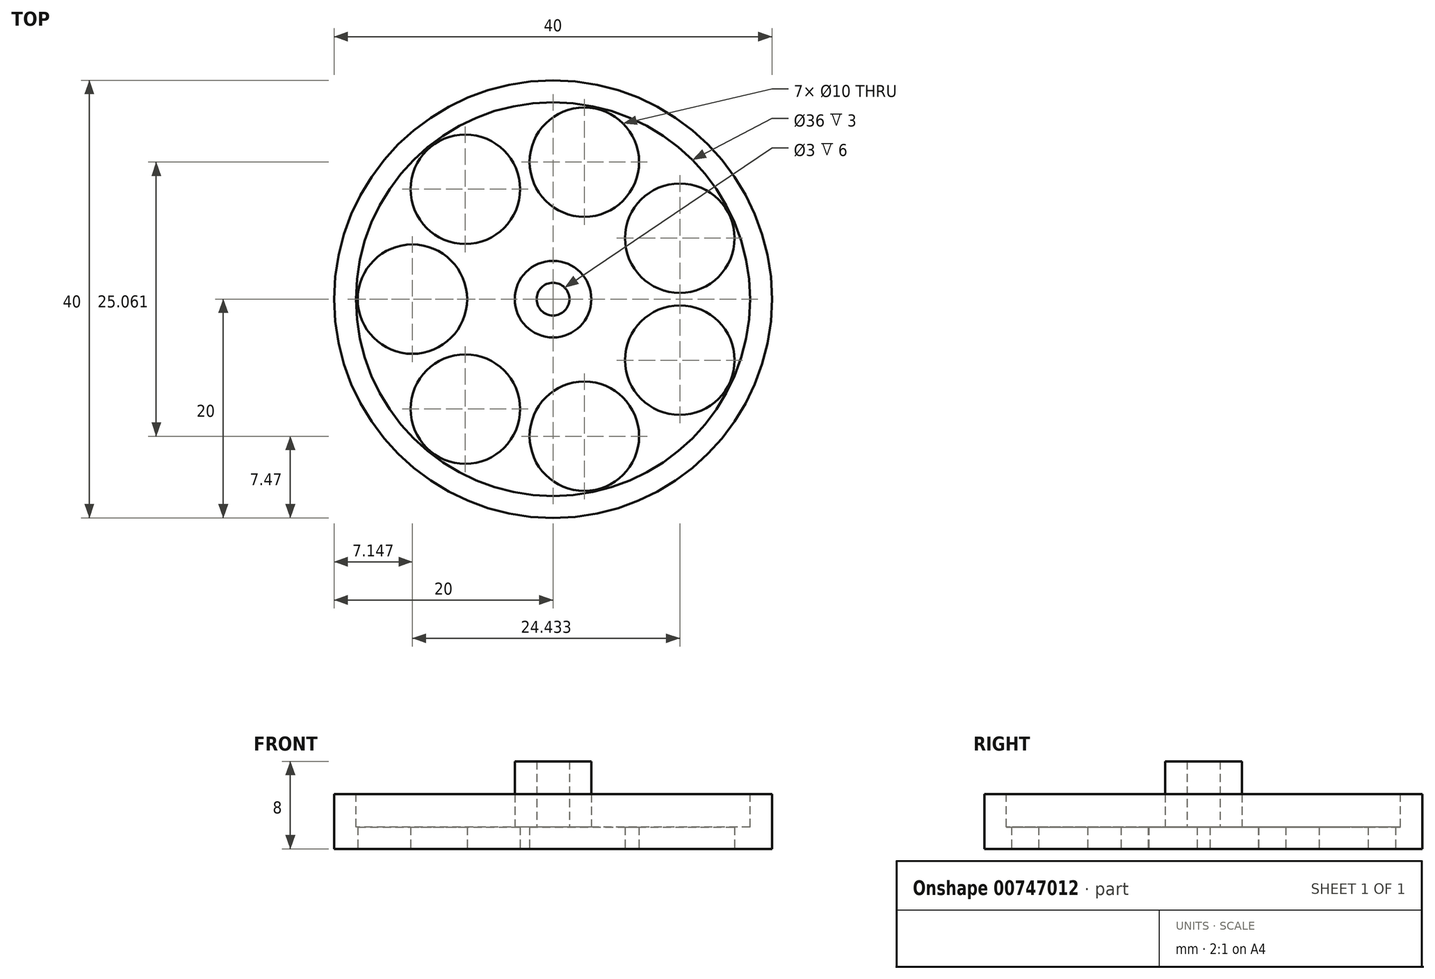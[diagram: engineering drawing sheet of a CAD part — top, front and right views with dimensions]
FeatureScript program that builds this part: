
annotation { "Feature Type Name" : "Feature", "Feature Type Description" : "" }
export const myFeature = defineFeature(function(context is Context, id is Id, definition is map)
    precondition{}
    {
        {
            var Q0;
            Q0=qCreatedBy(makeId("Top.planeOp"),FACE);
            var sketch = newSketch(context, id + "F0", { "sketchPlane" : qUnion([Q0])});
            skCircle(sketch, "E0", {"center": v(0, 0) * mm, "radius": 20 * mm});
            skSolve(sketch);
        }
        {
            var Q0;
            Q0=makeQuery(id+"F0.imprint","IMPRINT",FACE,{"disambiguationData":[TD([[makeQuery(id+"F0.imprint","IMPRINT",EDGE,{"derivedFrom":sQuery(id+"F0.wireOp",EDGE,"E0")}),1.0]])]});
            extrude(context, id + "F1", {"entities" : qUnion([Q0]), "depth" : 5 * mm, "offsetDistance" : 25 * mm});
        }
        {
            var Q0;
            Q0=makeQuery(id+"F1.opExtrude","CAP_FACE",FACE,{"disambiguationData":[OSD([sQuery(id+"F0.wireOp",EDGE,"E0")])],"isStart":false});
            var sketch = newSketch(context, id + "F2", { "sketchPlane" : qUnion([Q0])});
            skCircle(sketch, "E1", {"center": v(0, 0) * mm, "radius": 18 * mm});
            skSolve(sketch);
        }
        {
            var Q0;
            Q0=makeQuery(id+"F2.imprint","IMPRINT",FACE,{"disambiguationData":[TD([[makeQuery(id+"F2.imprint","IMPRINT",EDGE,{"derivedFrom":sQuery(id+"F2.wireOp",EDGE,"E1")}),1.0]])]});
            extrude(context, id + "F3", {"entities" : qUnion([Q0]), "operationType" : NewBodyOperationType.REMOVE, "oppositeDirection" : true, "depth" : 3 * mm, "offsetDistance" : 25 * mm});
        }
        {
            var Q0;
            Q0=makeQuery(id+"F3.boolean.opBoolean","COPY",FACE,{"derivedFrom":makeQuery(id+"F3.opExtrude","CAP_FACE",FACE,{"disambiguationData":[OSD([sQuery(id+"F2.wireOp",EDGE,"E1")])],"isStart":false})});
            var sketch = newSketch(context, id + "F4", { "sketchPlane" : qUnion([Q0])});
            skCircle(sketch, "E2", {"center": v(0, 0) * mm, "radius": 1.5 * mm});
            skCircle(sketch, "E3", {"center": v(0, 0) * mm, "radius": 3.5 * mm});
            skSolve(sketch);
        }
        {
            var Q0;
            Q0=makeQuery(id+"F4.imprint","IMPRINT",FACE,{"disambiguationData":[TD([[makeQuery(id+"F4.imprint","IMPRINT",EDGE,{"derivedFrom":sQuery(id+"F4.wireOp",EDGE,"E2")}),-1.0]])]});
            extrude(context, id + "F5", {"entities" : qUnion([Q0]), "operationType" : NewBodyOperationType.ADD, "depth" : 6 * mm, "offsetDistance" : 25 * mm});
        }
        {
            var Q0;
            Q0=makeQuery(id+"F1.opExtrude","CAP_FACE",FACE,{"disambiguationData":[OSD([sQuery(id+"F0.wireOp",EDGE,"E0")])],"isStart":true});
            var sketch = newSketch(context, id + "F6", { "sketchPlane" : qUnion([Q0])});
            skCircle(sketch, "E4", {"center": v(-12.85, 0) * mm, "radius": 5 * mm});
            skCircle(sketch, "E5.1.0", {"center": v(-8.01, -10.05) * mm, "radius": 5 * mm});
            skCircle(sketch, "E5.2.0", {"center": v(2.86, -12.53) * mm, "radius": 5 * mm});
            skCircle(sketch, "E5.3.0", {"center": v(11.58, -5.58) * mm, "radius": 5 * mm});
            skCircle(sketch, "E5.4.0", {"center": v(11.58, 5.58) * mm, "radius": 5 * mm});
            skPoint(sketch, "E5.center", {"position": v(0, 0) * mm});
            skCircle(sketch, "E6.1.5.0", {"center": v(2.86, 12.53) * mm, "radius": 5 * mm});
            skCircle(sketch, "E6.1.6.0", {"center": v(-8.01, 10.05) * mm, "radius": 5 * mm});
            skSolve(sketch);
        }
        {
            var Q0;
            Q0=qSketchRegion(id+"F6",true);
            extrude(context, id + "F7", {"entities" : qUnion([Q0]), "operationType" : NewBodyOperationType.REMOVE, "oppositeDirection" : true, "depth" : 2 * mm, "offsetDistance" : 25 * mm});
        }
    });
